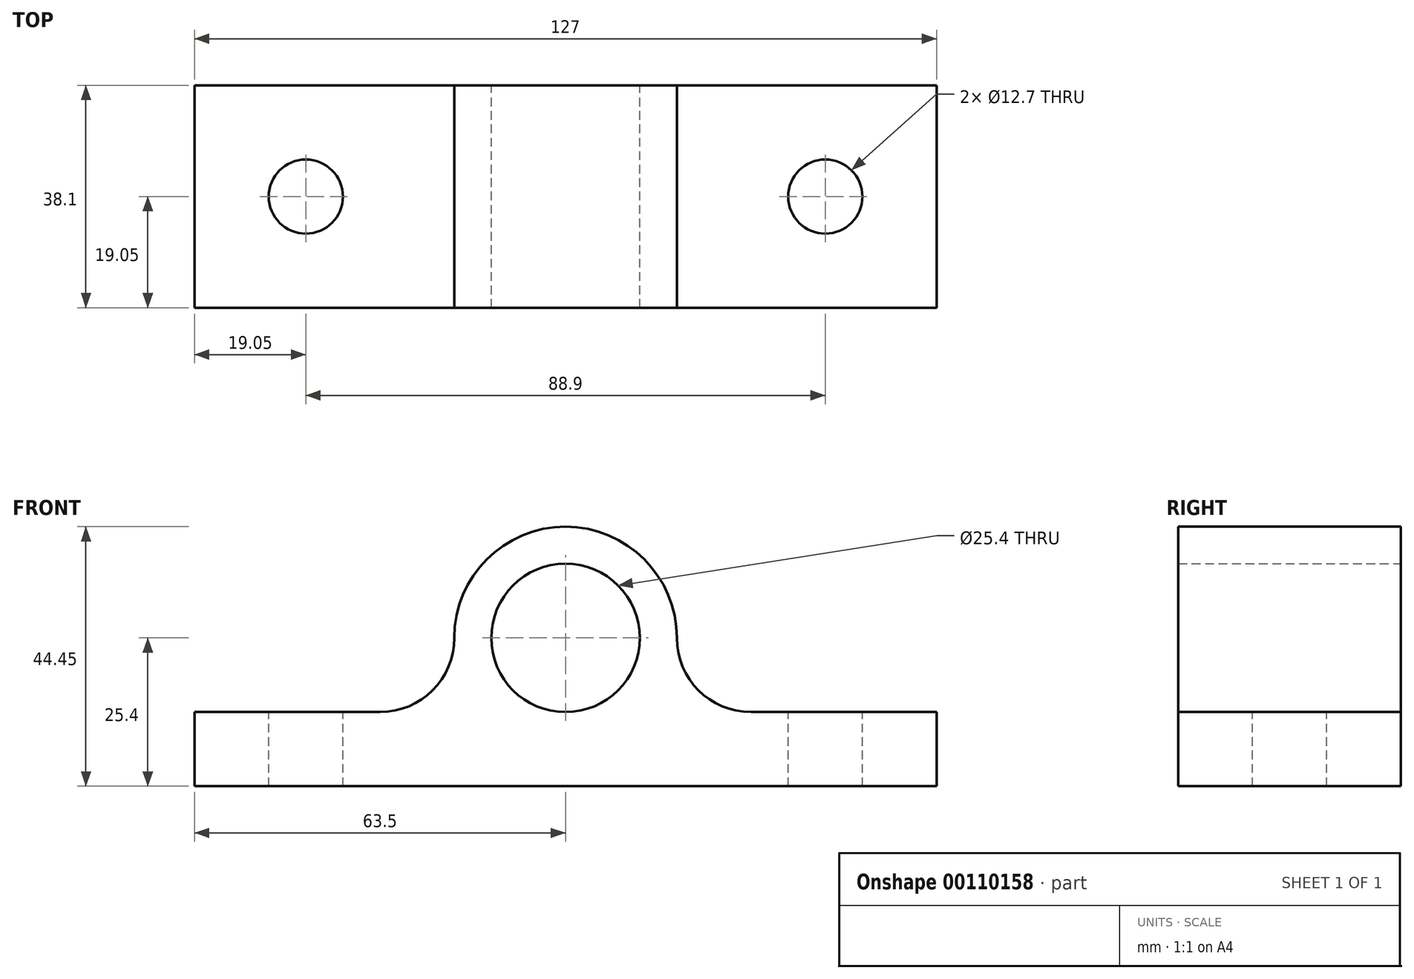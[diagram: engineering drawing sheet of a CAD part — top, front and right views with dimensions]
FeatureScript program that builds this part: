
annotation { "Feature Type Name" : "Feature", "Feature Type Description" : "" }
export const myFeature = defineFeature(function(context is Context, id is Id, definition is map)
    precondition{}
    {
        {
            var Q0;
            Q0=qCreatedBy(makeId("Front.planeOp"),FACE);
            var sketch = newSketch(context, id + "F0", { "sketchPlane" : qUnion([Q0])});
            skLineSegment(sketch, "E0", {"start": v(0, 0) * mm, "end": v(-63.5, 0) * mm});
            skLineSegment(sketch, "E1", {"start": v(-63.5, 0) * mm, "end": v(-63.5, 12.7) * mm});
            skLineSegment(sketch, "E2", {"start": v(-63.5, 12.7) * mm, "end": v(-31.75, 12.7) * mm});
            skLineSegment(sketch, "E3", {"start": v(31.75, 12.7) * mm, "end": v(63.5, 12.7) * mm});
            skLineSegment(sketch, "E4", {"start": v(63.5, 12.7) * mm, "end": v(63.5, 0) * mm});
            skLineSegment(sketch, "E5", {"start": v(63.5, 0) * mm, "end": v(0, 0) * mm});
            skPoint(sketch, "E6.visualSharp", {"position": v(-19.05, 12.7) * mm});
            skArc(sketch, "E6.filletArc", {"start": v(-31.75, 12.7) * mm, "mid": v(-22.77, 16.42) * mm, "end": v(-19.05, 25.4) * mm});
            skPoint(sketch, "E7.visualSharp", {"position": v(19.05, 12.7) * mm});
            skArc(sketch, "E7.filletArc", {"start": v(19.05, 25.4) * mm, "mid": v(22.77, 16.42) * mm, "end": v(31.75, 12.7) * mm});
            skArc(sketch, "E8", {"start": v(19.05, 25.4) * mm, "mid": v(0, 44.45) * mm, "end": v(-19.05, 25.4) * mm});
            skCircle(sketch, "E9", {"center": v(0, 25.4) * mm, "radius": 12.7 * mm});
            skSolve(sketch);
        }
        {
            var Q0;
            Q0=makeQuery(id+"F0.imprint","IMPRINT",FACE,{"disambiguationData":[TD([[makeQuery(id+"F0.imprint","IMPRINT",EDGE,{"derivedFrom":sQuery(id+"F0.wireOp",EDGE,"E0")}),-1.0]])]});
            extrude(context, id + "F1", {"entities" : qUnion([Q0]), "depth" : 38.1 * mm});
        }
        {
            var Q0;
            Q0=makeQuery(id+"F1.opExtrude","SWEPT_FACE",FACE,{"disambiguationData":[OSD([sQuery(id+"F0.wireOp",EDGE,"E3")])]});
            var sketch = newSketch(context, id + "F2", { "sketchPlane" : qUnion([Q0])});
            skLineSegment(sketch, "E10", {"start": v(63.5, 0) * mm, "end": v(44.45, 0) * mm, "construction": true});
            skLineSegment(sketch, "E11", {"start": v(44.45, 0) * mm, "end": v(44.45, -19.05) * mm, "construction": true});
            skCircle(sketch, "E12", {"center": v(44.45, -19.05) * mm, "radius": 6.35 * mm});
            skSolve(sketch);
        }
        {
            var Q0;
            Q0=makeQuery(id+"F2.imprint","IMPRINT",FACE,{"disambiguationData":[TD([[makeQuery(id+"F2.imprint","IMPRINT",EDGE,{"derivedFrom":sQuery(id+"F2.wireOp",EDGE,"E12")}),1.0]])]});
            extrude(context, id + "F3", {"entities" : qUnion([Q0]), "operationType" : NewBodyOperationType.REMOVE, "oppositeDirection" : true, "depth" : 25.4 * mm});
        }
        {
            var Q0;
            Q0=makeQuery(id+"F1.opExtrude","SWEPT_FACE",FACE,{"disambiguationData":[OSD([sQuery(id+"F0.wireOp",EDGE,"E2")])]});
            var sketch = newSketch(context, id + "F4", { "sketchPlane" : qUnion([Q0])});
            skLineSegment(sketch, "E13", {"start": v(-63.5, 0) * mm, "end": v(-44.45, 0) * mm, "construction": true});
            skLineSegment(sketch, "E14", {"start": v(-44.45, 0) * mm, "end": v(-44.45, -19.05) * mm, "construction": true});
            skCircle(sketch, "E15", {"center": v(-44.45, -19.05) * mm, "radius": 6.35 * mm});
            skSolve(sketch);
        }
        {
            var Q0;
            Q0=makeQuery(id+"F4.imprint","IMPRINT",FACE,{"disambiguationData":[TD([[makeQuery(id+"F4.imprint","IMPRINT",EDGE,{"derivedFrom":sQuery(id+"F4.wireOp",EDGE,"E15")}),1.0]])]});
            extrude(context, id + "F5", {"entities" : qUnion([Q0]), "operationType" : NewBodyOperationType.REMOVE, "oppositeDirection" : true, "depth" : 25.4 * mm});
        }
    });
